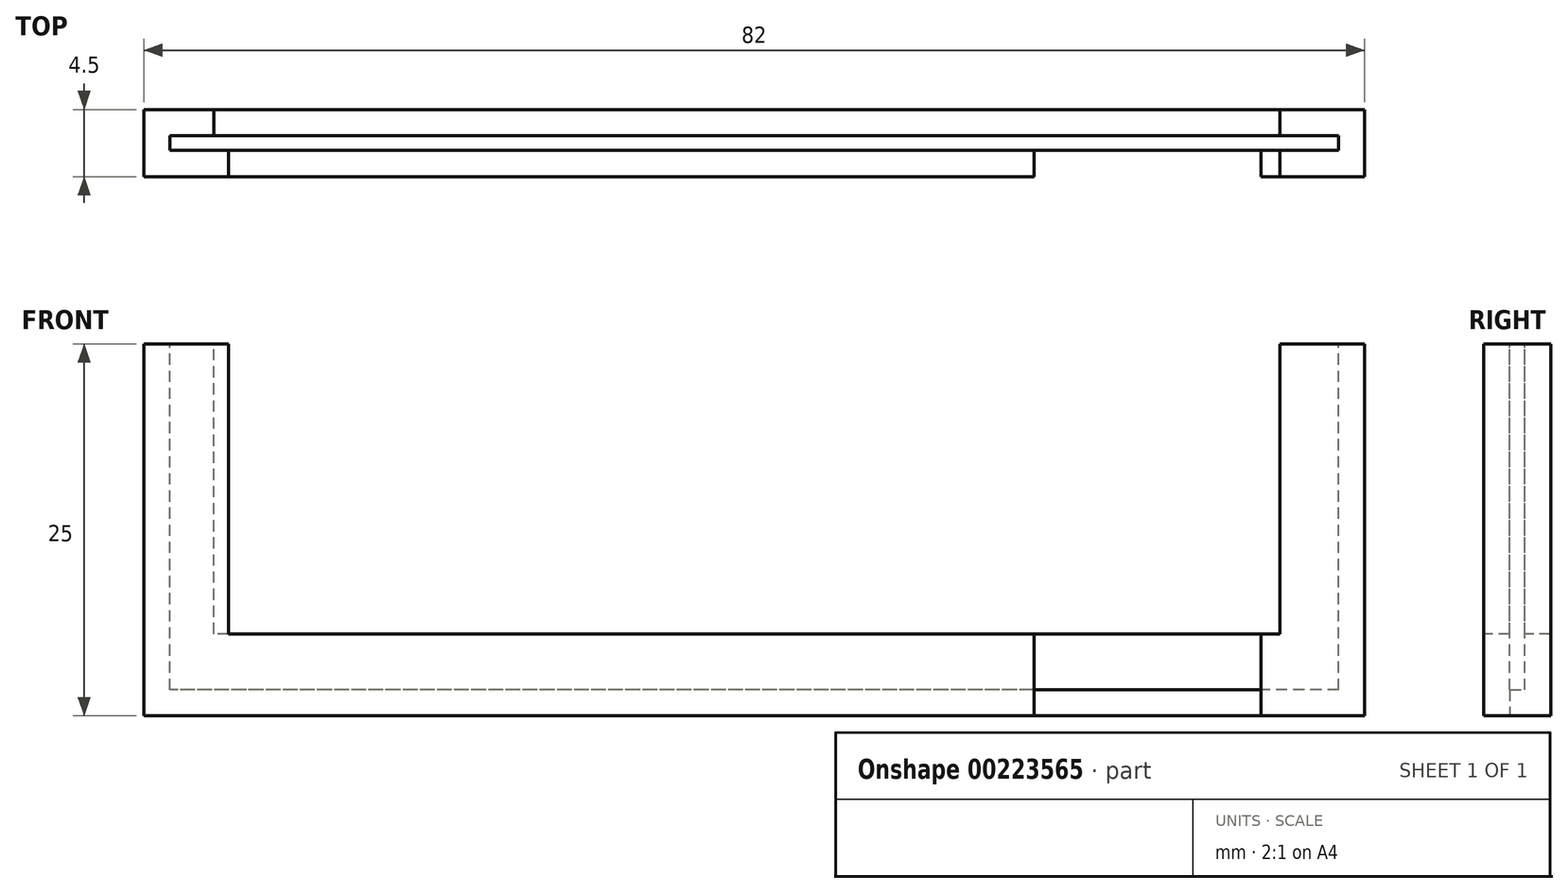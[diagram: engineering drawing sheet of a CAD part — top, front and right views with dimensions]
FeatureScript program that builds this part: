
annotation { "Feature Type Name" : "Feature", "Feature Type Description" : "" }
export const myFeature = defineFeature(function(context is Context, id is Id, definition is map)
    precondition{}
    {
        {
            var Q0;
            Q0=qCreatedBy(makeId("Front.planeOp"),FACE);
            var sketch = newSketch(context, id + "F0", { "sketchPlane" : qUnion([Q0])});
            skLineSegment(sketch, "E0.bottom", {"start": v(41, -12.5) * mm, "end": v(-41, -12.5) * mm});
            skLineSegment(sketch, "E0.top", {"start": v(41, 12.5) * mm, "end": v(-41, 12.5) * mm});
            skLineSegment(sketch, "E0.left", {"start": v(41, -12.5) * mm, "end": v(41, 12.5) * mm});
            skLineSegment(sketch, "E0.right", {"start": v(-41, -12.5) * mm, "end": v(-41, 12.5) * mm});
            skPoint(sketch, "E0.middle", {"position": v(0, 0) * mm});
            skSolve(sketch);
        }
        {
            var Q0;
            Q0=makeQuery(id+"F0.imprint","IMPRINT",FACE,{"disambiguationData":[TD([[makeQuery(id+"F0.imprint","IMPRINT",EDGE,{"derivedFrom":sQuery(id+"F0.wireOp",EDGE,"E0.bottom")}),-1.0]])]});
            extrude(context, id + "F1", {"entities" : qUnion([Q0]), "depth" : 4.5 * mm});
        }
        {
            var Q0;
            Q0=makeQuery(id+"F1.opExtrude","SWEPT_FACE",FACE,{"disambiguationData":[OSD([sQuery(id+"F0.wireOp",EDGE,"E0.top")])]});
            shell(context, id + "F2", {"entities" : qUnion([Q0]), "thickness" : 1.75 * mm});
        }
        {
            var Q0;
            Q0=makeQuery(id+"F1.opExtrude","CAP_FACE",FACE,{"disambiguationData":[OSD([sQuery(id+"F0.wireOp",EDGE,"E0.bottom"),sQuery(id+"F0.wireOp",EDGE,"E0.top"),sQuery(id+"F0.wireOp",EDGE,"E0.left"),sQuery(id+"F0.wireOp",EDGE,"E0.right")])],"isStart":false});
            var sketch = newSketch(context, id + "F3", { "sketchPlane" : qUnion([Q0])});
            skPoint(sketch, "E1.middle", {"position": v(0, 0) * mm});
            skLineSegment(sketch, "E2", {"start": v(-35.3, 12.5) * mm, "end": v(-35.3, -7) * mm});
            skLineSegment(sketch, "E3", {"start": v(-35.3, -7) * mm, "end": v(35.3, -7) * mm});
            skLineSegment(sketch, "E4", {"start": v(35.3, -7) * mm, "end": v(35.3, 12.5) * mm});
            skSolve(sketch);
        }
        {
            var Q0;
            {var subQ0=sQuery(id+"F3.wireOp",EDGE,"E2");Q0=makeQuery(id+"F3.imprint","IMPRINT",FACE,{"disambiguationData":[TD([[makeQuery(id+"F3.imprint","IMPRINT",EDGE,{"derivedFrom":subQ0}),1.0]])]});}
            extrude(context, id + "F4", {"entities" : qUnion([Q0]), "operationType" : NewBodyOperationType.REMOVE, "oppositeDirection" : true, "depth" : 50.8 * mm});
        }
        {
            var Q0;
            {var subQ0=sQuery(id+"F0.wireOp",EDGE,"E0.right");var subQ2=sQuery(id+"F0.wireOp",EDGE,"E0.top");Q0=makeQuery(id+"F4.boolean.opBoolean","SPLIT",FACE,{"disambiguationData":[TD([makeQuery(id+"F1.opExtrude","SWEPT_FACE",FACE,{"disambiguationData":[OSD([subQ0])]})])],"derivedFrom":makeQuery(id+"F1.opExtrude","SWEPT_FACE",FACE,{"disambiguationData":[OSD([subQ2])]})});}
            var sketch = newSketch(context, id + "F5", { "sketchPlane" : qUnion([Q0])});
            skLineSegment(sketch, "E5", {"start": v(-36.3, 0) * mm, "end": v(-36.3, -1.75) * mm});
            skLineSegment(sketch, "E6", {"start": v(-36.3, -1.75) * mm, "end": v(-35.3, -1.75) * mm});
            skLineSegment(sketch, "E7", {"start": v(-35.3, -1.75) * mm, "end": v(-35.3, 0) * mm});
            skLineSegment(sketch, "E8", {"start": v(-35.3, 0) * mm, "end": v(-36.3, 0) * mm});
            skSolve(sketch);
        }
        {
            var Q0;
            Q0=makeQuery(id+"F5.imprint","IMPRINT",FACE,{"disambiguationData":[TD([[makeQuery(id+"F5.imprint","IMPRINT",EDGE,{"derivedFrom":sQuery(id+"F5.wireOp",EDGE,"E5")}),1.0]])]});
            extrude(context, id + "F6", {"entities" : qUnion([Q0]), "operationType" : NewBodyOperationType.REMOVE, "oppositeDirection" : true, "depth" : 19.5 * mm});
        }
        {
            var Q0;
            Q0=makeQuery(id+"F1.opExtrude","CAP_FACE",FACE,{"disambiguationData":[OSD([sQuery(id+"F0.wireOp",EDGE,"E0.bottom"),sQuery(id+"F0.wireOp",EDGE,"E0.top"),sQuery(id+"F0.wireOp",EDGE,"E0.left"),sQuery(id+"F0.wireOp",EDGE,"E0.right")])],"isStart":false});
            var sketch = newSketch(context, id + "F7", { "sketchPlane" : qUnion([Q0])});
            skLineSegment(sketch, "E9", {"start": v(18.79, -7) * mm, "end": v(18.79, -12.5) * mm});
            skLineSegment(sketch, "E10", {"start": v(18.79, -12.5) * mm, "end": v(34.03, -12.5) * mm});
            skLineSegment(sketch, "E11", {"start": v(34.03, -12.5) * mm, "end": v(34.03, -7) * mm});
            skLineSegment(sketch, "E12", {"start": v(34.03, -7) * mm, "end": v(18.79, -7) * mm});
            skSolve(sketch);
        }
        {
            var Q0;
            Q0=makeQuery(id+"F7.imprint","IMPRINT",FACE,{"disambiguationData":[TD([[makeQuery(id+"F7.imprint","IMPRINT",EDGE,{"derivedFrom":sQuery(id+"F7.wireOp",EDGE,"E9")}),1.0]])]});
            extrude(context, id + "F8", {"entities" : qUnion([Q0]), "operationType" : NewBodyOperationType.REMOVE, "oppositeDirection" : true, "depth" : 1.75 * mm});
        }
    });
